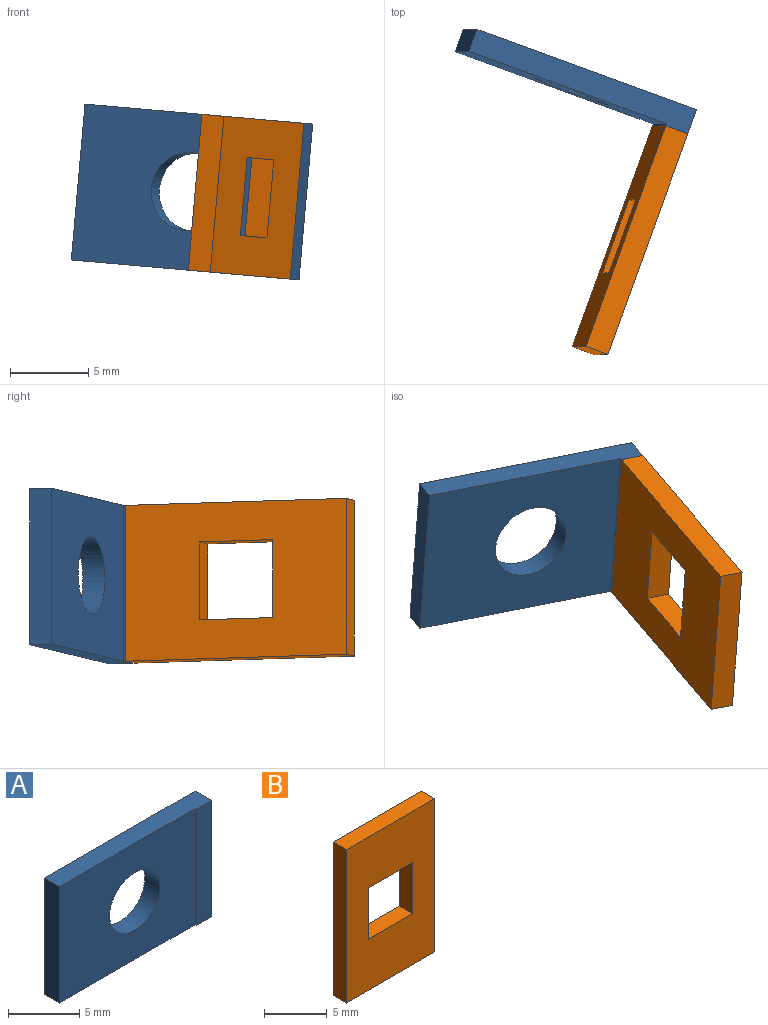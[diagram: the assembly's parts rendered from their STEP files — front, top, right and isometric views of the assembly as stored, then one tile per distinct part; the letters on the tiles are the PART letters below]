
ASSEMBLY  parts=2 mates=1
PART A: 9 faces, bbox 15x1.7x10 mm
  f0: plane 13.5x10mm, normal (0,-1,0), area 115.4mm2, adj f1,f3,f4,f6,f7
  f1: plane 15x1.65mm, normal (0,0,-1), area 22.7mm2, adj f0,f2,f4,f5,f7,f8
  f2: plane 10x1.65mm, normal (1,0,0), area 16.5mm2, adj f1,f3,f5,f8
  f3: plane 15x1.65mm, normal (0,0,1), area 22.7mm2, adj f0,f2,f4,f5,f7,f8
  f4: plane 10x1.5mm, normal (-1,0,0), area 15mm2, adj f0,f1,f3,f5
  f5: plane 15x10mm, normal (0,1,0), area 130.4mm2, adj f1,f2,f3,f4,f6
  f6: cylinder r=2.5mm len=5mm, axis (0,-1,0), area 23.6mm2, adj f0,f5
  f7: plane 10x0.15mm, normal (-1,0,0), area 1.5mm2, adj f0,f1,f3,f8
  f8: plane 10x1.5mm, normal (0,-1,0), area 15mm2, adj f1,f2,f3,f7
PART B: 10 faces, bbox 10x1.5x15 mm
  f0: plane 15x10mm, normal (0,-1,0), area 125mm2, adj f2,f3,f4,f5,f6,f7,f8,f9
  f1: plane 15x10mm, normal (0,1,0), area 125mm2, adj f2,f3,f4,f5,f6,f7,f8,f9
  f2: plane 10x1.5mm, normal (0,0,-1), area 15mm2, adj f0,f1,f3,f5
  f3: plane 15x1.5mm, normal (1,0,0), area 22.5mm2, adj f0,f1,f2,f4
  f4: plane 10x1.5mm, normal (0,0,1), area 15mm2, adj f0,f1,f3,f5
  f5: plane 15x1.5mm, normal (-1,0,0), area 22.5mm2, adj f0,f1,f2,f4
  f6: plane 5x1.5mm, normal (0,0,1), area 7.5mm2, adj f0,f1,f7,f9
  f7: plane 5x1.5mm, normal (-1,0,0), area 7.5mm2, adj f0,f1,f6,f8
  f8: plane 5x1.5mm, normal (0,0,-1), area 7.5mm2, adj f0,f1,f7,f9
  f9: plane 5x1.5mm, normal (1,0,0), area 7.5mm2, adj f0,f1,f6,f8
PLACE A rot(axis=(-0.04,0.24,-0.97),20.6deg) t=(-6.36,1.77,-10.87)mm
PLACE B rot(axis=(0.53,-0.69,0.49),105.7deg) t=(-3.87,-8.88,-11.09)mm
MATE fastened A.f8 <-> B.f2  axis (-0.34,-0.94,0.03) through (-0.61,-2.09,-11.38)mm
